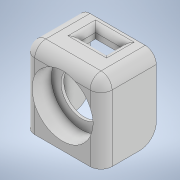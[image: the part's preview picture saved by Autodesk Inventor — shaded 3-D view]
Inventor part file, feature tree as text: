
AUTODESK INVENTOR PART (.ipt)
format: ipt  version: 2021 (Build 250183000, 183)  size: 192,000 bytes
history: native  units: mm
features: extrude x4, sketch x4, fillet x3, projected_geometry x2
ambient origin geometry x8: Origin, YZ Plane, XZ Plane, XY Plane, X Axis, Y Axis, Z Axis, Center Point
bodies: Solid1 (feature_tree)
feature tree (13):
  extrude  "Extrusion1"  Depth=20.0mm
  extrude  "Extrusion2"  Depth=4.0mm
  extrude  "Extrusion3"  Depth=4.0mm
  fillet  "Fillet1"  Radius=1.0mm
  fillet  "Fillet2"  Radius=22.0mm
  extrude  "Extrusion4"  Depth=2.0mm TaperAngle=0.0deg
  fillet  "Fillet3"  Radius=4.0mm
  sketch  "Sketch1"  dims[d0=15.0mm d1=20.0mm]
  sketch  "Sketch2"  dims[d2=20.0mm d3=4.0mm]
  projected_geometry  "Projected Loop1"
  sketch  "Sketch3"  dims[d4=4.0mm d5=4.0mm d6=1.0mm d7=0.0mm d8=22.0mm]
  projected_geometry  "Projected Loop2"
  sketch  "Sketch4"  dims[d9=4.0mm d10=7.0mm d11=0.0mm d12=4.0mm d13=12.0mm d14=0.0mm d15=6.0mm d16=4.0mm d17=10.0mm d18=6.0mm d19=3.0mm d20=5.0mm d21=10.0mm d22=0.0mm d23=2.0mm]
